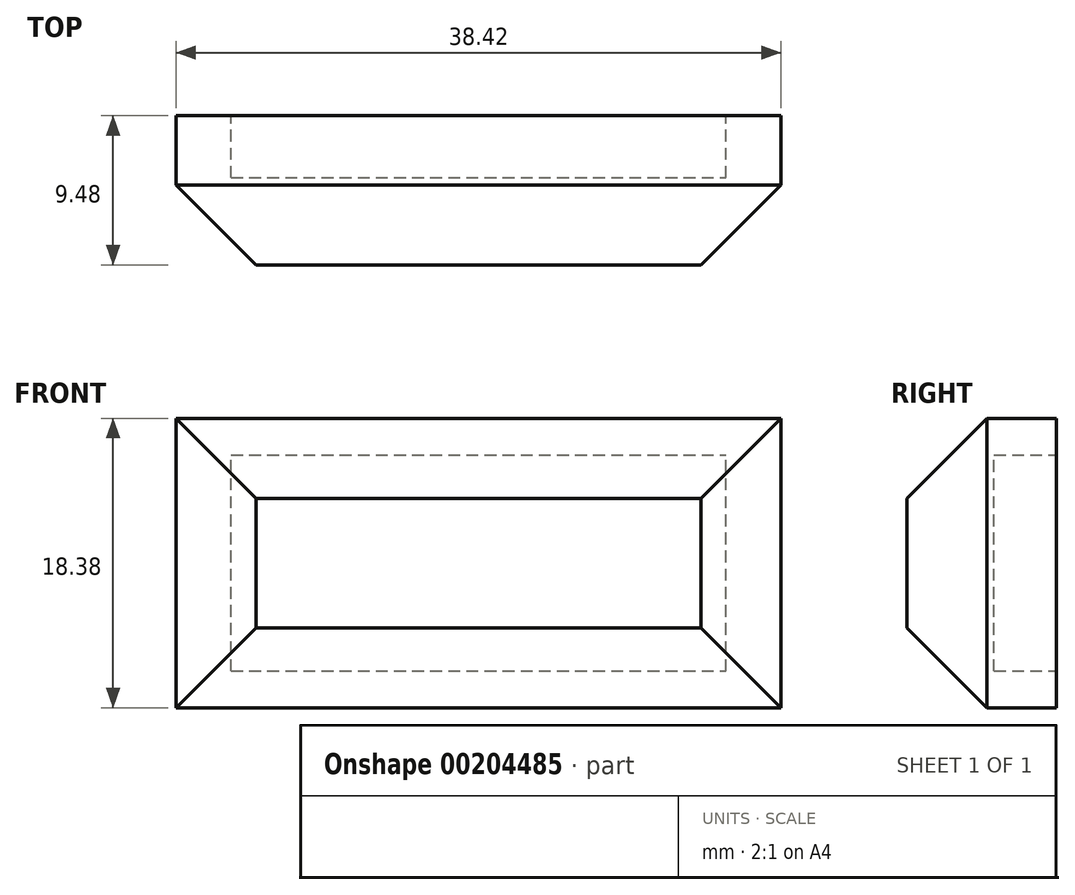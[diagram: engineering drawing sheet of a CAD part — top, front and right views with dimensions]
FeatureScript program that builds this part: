
annotation { "Feature Type Name" : "Feature", "Feature Type Description" : "" }
export const myFeature = defineFeature(function(context is Context, id is Id, definition is map)
    precondition{}
    {
        {
            var Q0;
            Q0=qCreatedBy(makeId("Front.planeOp"),FACE);
            var sketch = newSketch(context, id + "F0", { "sketchPlane" : qUnion([Q0])});
            skLineSegment(sketch, "E0.bottom", {"start": v(19.2, 9.2) * mm, "end": v(-19.2, 9.2) * mm});
            skLineSegment(sketch, "E0.top", {"start": v(19.2, -9.2) * mm, "end": v(-19.2, -9.2) * mm});
            skLineSegment(sketch, "E0.left", {"start": v(19.2, 9.2) * mm, "end": v(19.2, -9.2) * mm});
            skLineSegment(sketch, "E0.right", {"start": v(-19.2, 9.2) * mm, "end": v(-19.2, -9.2) * mm});
            skPoint(sketch, "E0.middle", {"position": v(0, 0) * mm});
            skSolve(sketch);
        }
        {
            var Q0;
            Q0 = qSketchRegion(id + "F0", true);
            extrude(context, id + "F4", {"entities" : qUnion([Q0]), "depth" : 9.48 * mm});
        }
        {
            var Q0;
            Q0=makeQuery(id+"F4.opExtrude","CAP_FACE",FACE,{"disambiguationData":[OSD([sQuery(id+"F0.wireOp",EDGE,"E0.bottom"),sQuery(id+"F0.wireOp",EDGE,"E0.top"),sQuery(id+"F0.wireOp",EDGE,"E0.left"),sQuery(id+"F0.wireOp",EDGE,"E0.right")])],"isStart":false});
            chamfer(context, id + "F1", {"entities" : qUnion([Q0]), "width" : 5.08 * mm, "tangentPropagation" : true});
        }
        {
            var Q0;
            Q0=makeQuery(id+"F4.opExtrude","CAP_FACE",FACE,{"disambiguationData":[OSD([sQuery(id+"F0.wireOp",EDGE,"E0.bottom"),sQuery(id+"F0.wireOp",EDGE,"E0.top"),sQuery(id+"F0.wireOp",EDGE,"E0.left"),sQuery(id+"F0.wireOp",EDGE,"E0.right")])],"isStart":true});
            var sketch = newSketch(context, id + "F2", { "sketchPlane" : qUnion([Q0])});
            skLineSegment(sketch, "E1.bottom", {"start": v(15.72, -6.86) * mm, "end": v(-15.72, -6.86) * mm});
            skLineSegment(sketch, "E1.top", {"start": v(15.72, 6.86) * mm, "end": v(-15.72, 6.86) * mm});
            skLineSegment(sketch, "E1.left", {"start": v(15.72, -6.86) * mm, "end": v(15.72, 6.86) * mm});
            skLineSegment(sketch, "E1.right", {"start": v(-15.72, -6.86) * mm, "end": v(-15.72, 6.86) * mm});
            skPoint(sketch, "E1.middle", {"position": v(0, 0) * mm});
            skSolve(sketch);
        }
        {
            var Q0;
            Q0 = qSketchRegion(id + "F2", true);
            extrude(context, id + "F3", {"entities" : qUnion([Q0]), "operationType" : NewBodyOperationType.REMOVE, "oppositeDirection" : true, "depth" : 3.94 * mm});
        }
    });
